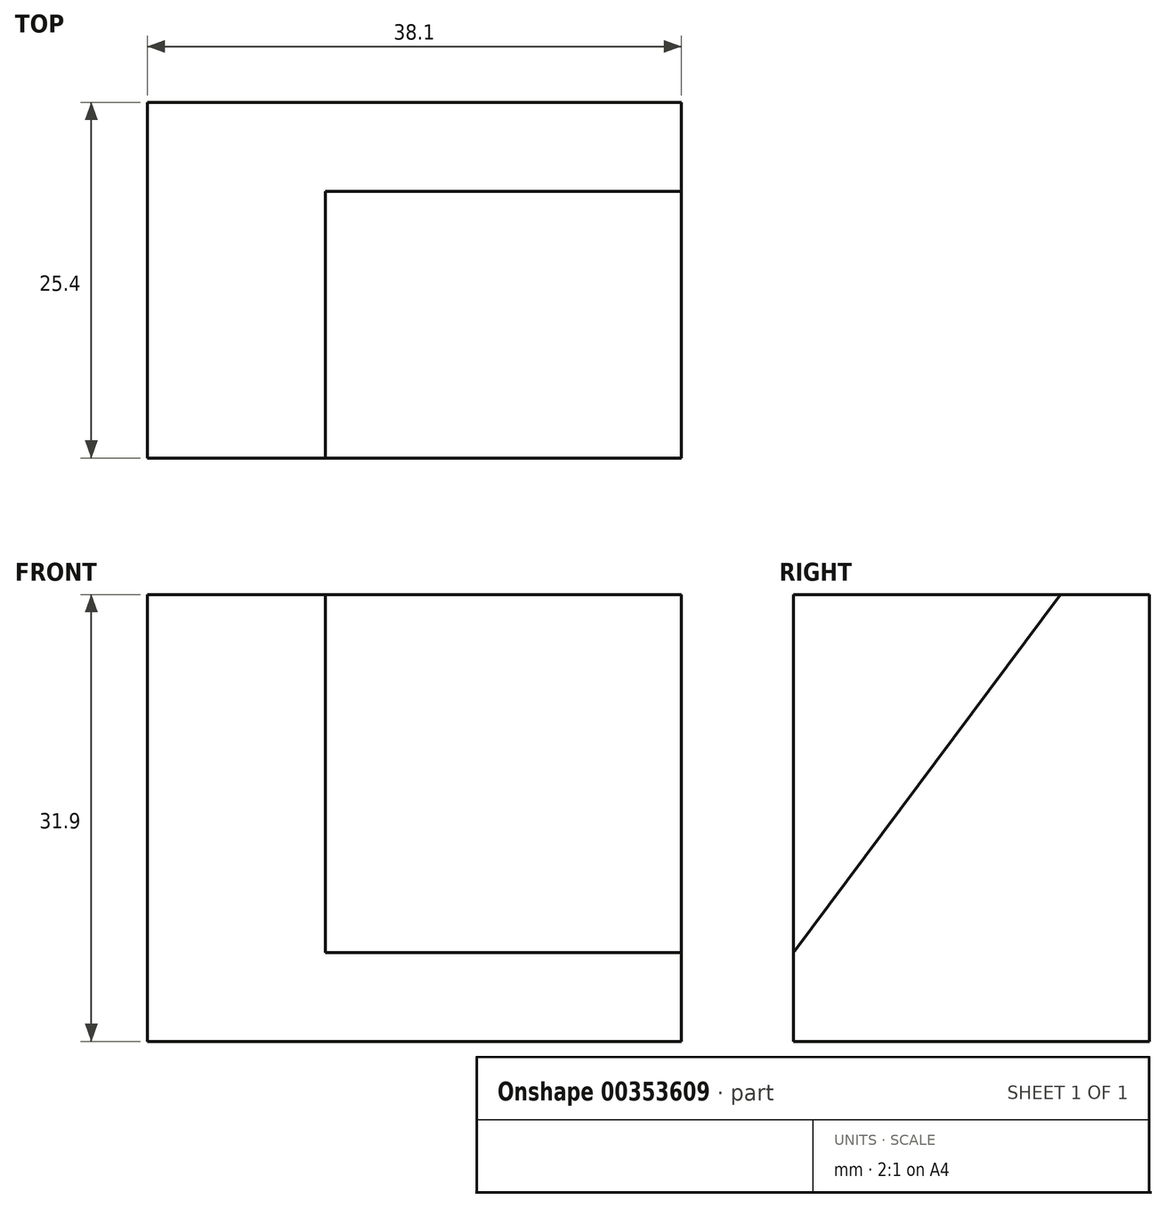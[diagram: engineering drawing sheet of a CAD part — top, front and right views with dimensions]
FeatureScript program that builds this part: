
annotation { "Feature Type Name" : "Feature", "Feature Type Description" : "" }
export const myFeature = defineFeature(function(context is Context, id is Id, definition is map)
    precondition{}
    {
        {
            var Q0;
            Q0=qCreatedBy(makeId("Right.planeOp"),FACE);
            var sketch = newSketch(context, id + "F0", { "sketchPlane" : qUnion([Q0])});
            skLineSegment(sketch, "E0", {"start": v(0, 0) * mm, "end": v(25.4, 0) * mm});
            skLineSegment(sketch, "E1", {"start": v(25.4, 0) * mm, "end": v(25.4, 31.9) * mm});
            skLineSegment(sketch, "E2", {"start": v(0, 0) * mm, "end": v(0, 6.35) * mm});
            skLineSegment(sketch, "E3", {"start": v(25.4, 31.9) * mm, "end": v(19.05, 31.9) * mm});
            skLineSegment(sketch, "E4", {"start": v(19.05, 31.9) * mm, "end": v(0, 6.35) * mm});
            skSolve(sketch);
        }
        {
            var Q0;
            Q0=makeQuery(id+"F0.imprint","IMPRINT",FACE,{"disambiguationData":[TD([[makeQuery(id+"F0.imprint","IMPRINT",EDGE,{"derivedFrom":sQuery(id+"F0.wireOp",EDGE,"E0")}),1.0]])]});
            extrude(context, id + "F1", {"entities" : qUnion([Q0]), "depth" : 38.1 * mm});
        }
        {
            var Q0;
            Q0=makeQuery(id+"F1.opExtrude","CAP_FACE",FACE,{"disambiguationData":[OSD([sQuery(id+"F0.wireOp",EDGE,"E0"),sQuery(id+"F0.wireOp",EDGE,"E1"),sQuery(id+"F0.wireOp",EDGE,"E2"),sQuery(id+"F0.wireOp",EDGE,"E3"),sQuery(id+"F0.wireOp",EDGE,"E4")])],"isStart":true});
            var sketch = newSketch(context, id + "F2", { "sketchPlane" : qUnion([Q0])});
            skLineSegment(sketch, "E5", {"start": v(-19.05, 31.9) * mm, "end": v(0, 31.9) * mm});
            skLineSegment(sketch, "E6", {"start": v(0, 31.9) * mm, "end": v(0, 6.35) * mm});
            skSolve(sketch);
        }
        {
            var Q0;
            Q0=makeQuery(id+"F2.imprint","IMPRINT",FACE,{"disambiguationData":[TD([[makeQuery(id+"F2.imprint","IMPRINT",EDGE,{"derivedFrom":sQuery(id+"F2.wireOp",EDGE,"E5")}),-1.0]])]});
            extrude(context, id + "F3", {"entities" : qUnion([Q0]), "operationType" : NewBodyOperationType.ADD, "oppositeDirection" : true, "depth" : 12.7 * mm});
        }
    });
